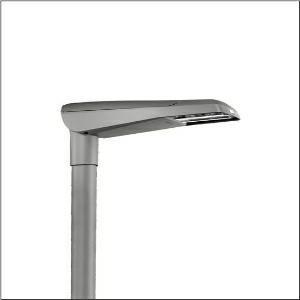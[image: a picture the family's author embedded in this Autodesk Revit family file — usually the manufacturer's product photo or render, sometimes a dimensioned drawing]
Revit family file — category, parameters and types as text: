
# Revit family: streetlight_sl_11_iq_micro___p1_0a_5xc1cc1f08ce_9736
name_source: partatom
category: Lighting Fixtures
units: mm (PartAtom-declared; Revit-internal decimal feet)

## family parameters
Cut with Voids When Loaded = No
Host = Face
Light Source = No
Part Type = Normal
Room Calculation Point = No
Round Connector Dimension = Use Diameter
Shared = No

## types (1)
- --- (1 x LED, 1360 lm, 12.2 W, 2200K)
    Apparent Load = 12 VA
    CIE Flux Codes = 29 63 93 100 100
    Color Rendering = 70
    Color Temperature = 2200K
    Default Elevation = 1800 mm
    Description = Streetlight SL 11 iQ micro, mast luminaire, primary light control with 3 zone facetted reflector, of plastic, silver coated, highly specular, primary optical cover: cover, of PMMA, transparent, light distribution: P1.0a, light emission: direct distribution, primary light characteristic: asymmetric, installation type: post-top, side-entry, lamps: LED, High Power LED, rated values: 1.600lm | 12W | 133,3lm/W (begin service life); end service life: 1.600lm | 12,2W; at 50% lumin. flux: 800lm | 6,7W | 119,4lm/W, colour temperature: 2200/2700/3000/4000K, colour rendering: CRI > 70, light colour: 722/727/730/740, light setting 1 begin service life: 100% | 1.600lm | 12W | 133,3lm/W | 3.000K, light setting 1 end service life: 12,2W, further light settings possible, control: Street-Remote, Auto-Match, Temp-Guard, Lumen-Switch, Night-Set, Smart-Wire, Light-Fading, Desk-Remote (wireless, voltage-free reading and setting of iQ features in the workshop via application-optimized NFC function/RFID function), optimised constant luminous flux control (CLO 2.0), with cable H07RN-F 5x 1.5mm², mains connection: 220..240V, AC, 50/60Hz, connection cable pre-assembled, cable length: 5,5m, luminaire housing, of diecast aluminium, powder-coated, Siteco® metallic grey (DB 702S), please order mast flange separately, inclination adjustable without tools: 0°, 5°, 10°, 15° (post-top) | 0°, -5°, -10°, -15° (side-entry), sealing non-destructively replaceable, multi-level sealing system, length: 600mm, width: 174mm, height: 116mm, mast flange for spigot size: 42mm (side-entry): 5XC10008XM4, 60/48mm (side-entry/post-top): 5XC10108XM2, 76/60mm (side-entry/post-top): 5XC10108XM1, equipment: standard, protection rating (complete): IP66, insulation class (complete): insulation class II (safety insulation), certification: CE, ENEC, ENEC+, VDE, impact resistance: IK10, permissible operating ambient temperature for outdoor applications: -25..+50°C, standard-compliant lighting for roads and squares, Environmental Product Declaration (EPD) tested and certified by an independent institute, packaging unit: 1 piece

Light Distribution: P1.0a
    Height = 116 mm
    Lamp = 1 x LED
    Lamp Light Flux = 1360 lm
    Lamp Power = 12.2 W
    Lamp count = 1
    Length = 600 mm
    Luminous efficacy = 111 lm/W
    Manufacturer = Siteco
    ModVariant = No
    Model = 5XC1CC1F08CE
    Number of Poles = 1
    OnlyDefault = Yes
    Power Factor = 1
    Product Name = Streetlight SL 11 iQ micro | P1.0a
    Product group = mast luminaire | pylon top
    ProductGroupID = 6100
    Protection Class = Protection class II
    Protection Degree = IP 66
    RLX_Detail_Level = 1
    RLX_Emergency_Light_Flux = 0 lm
    RLX_Emergency_Type = 0
    RLX_Emergency_Type_DB = No
    RlxData = <blob elided: 58045 chars, md5=8c43811e>
    Socket = socket
    Standby Power = 0 W
    System Light Flux = 1360 lm
    System Power = 12 W
    Type Comments = individual setting: luminous flux: 100 % | dim-lin: 254 | 318 mA
    Type Image = l_1006566.jpg
    URL = http://relux.com
    VarID = @adj_055699
    Voltage = 0 V
    Weight = 0.00 kg
    Width = 174 mm

## geometry (parser evidence)
native form markers: Blend x4, Sweep x11
no freeform markers — native parametric forms only
